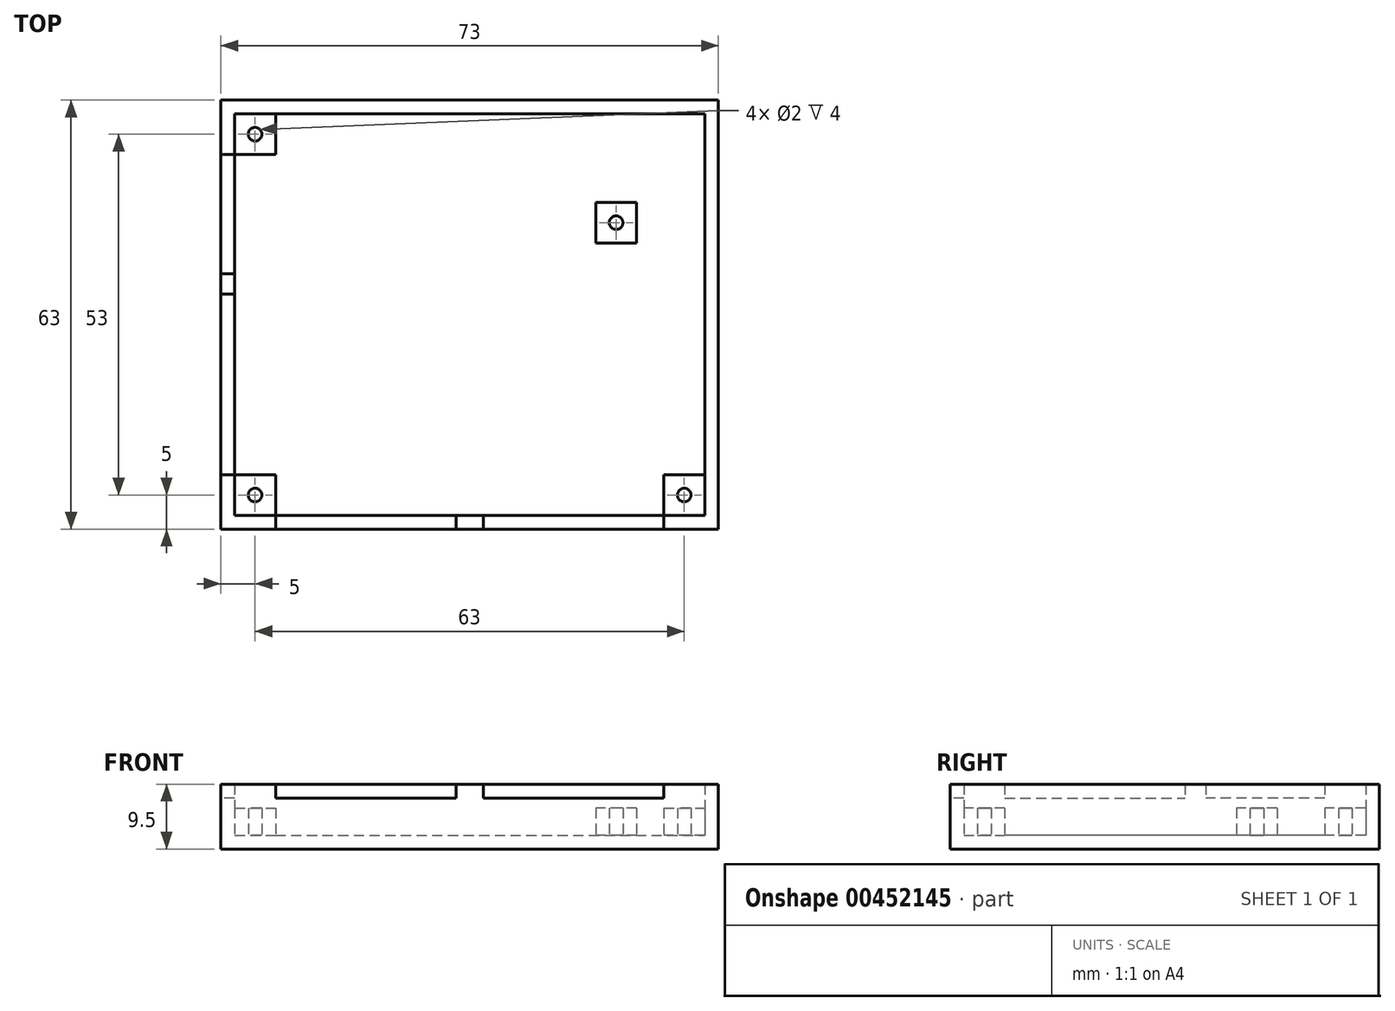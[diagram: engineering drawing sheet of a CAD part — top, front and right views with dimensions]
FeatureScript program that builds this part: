
annotation { "Feature Type Name" : "Feature", "Feature Type Description" : "" }
export const myFeature = defineFeature(function(context is Context, id is Id, definition is map)
    precondition{}
    {
        {
            assignVariable(context, id + "F0", {"name" : "SCREW_BOX_H", "anyValue" : 4});
        }
        {
            assignVariable(context, id + "F1", {"name" : "GPIO_H", "anyValue" : 2.5 * mm});
        }
        {
            assignVariable(context, id + "F2", {"name" : "PERIPHERALS_BOTTOM", "anyValue" : 7 * mm});
        }
        {
            var Q0;
            Q0=qCreatedBy(makeId("Top.planeOp"),FACE);
            var sketch = newSketch(context, id + "F3", { "sketchPlane" : qUnion([Q0])});
            skLineSegment(sketch, "E0.bottom", {"start": v(-34.5, 29.5) * mm, "end": v(34.5, 29.5) * mm});
            skLineSegment(sketch, "E0.top", {"start": v(-34.5, -29.5) * mm, "end": v(34.5, -29.5) * mm});
            skLineSegment(sketch, "E0.left", {"start": v(-34.5, 29.5) * mm, "end": v(-34.5, -29.5) * mm});
            skLineSegment(sketch, "E0.right", {"start": v(34.5, 29.5) * mm, "end": v(34.5, -29.5) * mm});
            skPoint(sketch, "E0.middle", {"position": v(0, 0) * mm});
            skLineSegment(sketch, "E1.0", {"start": v(-36.5, 31.5) * mm, "end": v(36.5, 31.5) * mm});
            skLineSegment(sketch, "E1.1", {"start": v(-36.5, 31.5) * mm, "end": v(-36.5, -31.5) * mm});
            skLineSegment(sketch, "E1.2", {"start": v(-36.5, -31.5) * mm, "end": v(36.5, -31.5) * mm});
            skLineSegment(sketch, "E1.3", {"start": v(36.5, 31.5) * mm, "end": v(36.5, -31.5) * mm});
            skSolve(sketch);
        }
        {
            var Q0;
            Q0=makeQuery(id+"F3.imprint","IMPRINT",FACE,{"disambiguationData":[TD([[makeQuery(id+"F3.imprint","IMPRINT",EDGE,{"derivedFrom":sQuery(id+"F3.wireOp",EDGE,"E0.bottom")}),1.0]])]});
            extrude(context, id + "F4", {"entities" : qUnion([Q0]), "depth" : getVariable(context, 'PERIPHERALS_BOTTOM') + getVariable(context, 'GPIO_H')});
        }
        {
            var Q0;
            Q0=makeQuery(id+"F3.imprint","IMPRINT",FACE,{"disambiguationData":[TD([[makeQuery(id+"F3.imprint","IMPRINT",EDGE,{"derivedFrom":sQuery(id+"F3.wireOp",EDGE,"E0.bottom")}),-1.0]])]});
            extrude(context, id + "F5", {"entities" : qUnion([Q0]), "operationType" : NewBodyOperationType.ADD, "depth" : 2 * mm});
        }
        {
            var Q0;
            Q0=makeQuery(id+"F5.opExtrude","CAP_FACE",FACE,{"disambiguationData":[OSD([sQuery(id+"F3.wireOp",EDGE,"E0.bottom"),sQuery(id+"F3.wireOp",EDGE,"E0.top"),sQuery(id+"F3.wireOp",EDGE,"E0.left"),sQuery(id+"F3.wireOp",EDGE,"E0.right")])],"isStart":false});
            var sketch = newSketch(context, id + "F6", { "sketchPlane" : qUnion([Q0])});
            skLineSegment(sketch, "E2.bottom", {"start": v(34.5, -29.5) * mm, "end": v(28.5, -29.5) * mm});
            skLineSegment(sketch, "E2.top", {"start": v(34.5, -23.5) * mm, "end": v(28.5, -23.5) * mm});
            skLineSegment(sketch, "E2.left", {"start": v(34.5, -29.5) * mm, "end": v(34.5, -23.5) * mm});
            skLineSegment(sketch, "E2.right", {"start": v(28.5, -29.5) * mm, "end": v(28.5, -23.5) * mm});
            skLineSegment(sketch, "E3.MirrorCS", {"start": v(-28.5, -29.5) * mm, "end": v(-28.5, -23.5) * mm});
            skLineSegment(sketch, "E4.MirrorCS", {"start": v(-34.5, -23.5) * mm, "end": v(-28.5, -23.5) * mm});
            skLineSegment(sketch, "E5.MirrorCS", {"start": v(-34.5, -29.5) * mm, "end": v(-34.5, -23.5) * mm});
            skLineSegment(sketch, "E6.MirrorCS", {"start": v(-34.5, -29.5) * mm, "end": v(-28.5, -29.5) * mm});
            skLineSegment(sketch, "E7.MirrorCS", {"start": v(-34.5, 23.5) * mm, "end": v(-28.5, 23.5) * mm});
            skLineSegment(sketch, "E8.MirrorCS", {"start": v(-28.5, 29.5) * mm, "end": v(-28.5, 23.5) * mm});
            skLineSegment(sketch, "E9.MirrorCS", {"start": v(-34.5, 29.5) * mm, "end": v(-28.5, 29.5) * mm});
            skLineSegment(sketch, "E10.MirrorCS", {"start": v(-34.5, 29.5) * mm, "end": v(-34.5, 23.5) * mm});
            skCircle(sketch, "E11", {"center": v(31.5, -26.5) * mm, "radius": 1 * mm});
            skPoint(sketch, "E11.centerSnap0", {"position": v(28.5, -26.5) * mm});
            skPoint(sketch, "E11.centerSnap1", {"position": v(31.5, -23.5) * mm});
            skCircle(sketch, "E12.MirrorC", {"center": v(-31.5, -26.5) * mm, "radius": 1 * mm});
            skCircle(sketch, "E13.MirrorC", {"center": v(-31.5, 26.5) * mm, "radius": 1 * mm});
            skLineSegment(sketch, "E14.top", {"start": v(34.5, 16.5) * mm, "end": v(24.5, 16.5) * mm, "construction": true});
            skLineSegment(sketch, "E14.right", {"start": v(24.5, 29.5) * mm, "end": v(24.5, 16.5) * mm, "construction": true});
            skLineSegment(sketch, "E15.bottom", {"start": v(24.5, 16.5) * mm, "end": v(18.5, 16.5) * mm});
            skLineSegment(sketch, "E15.top", {"start": v(24.5, 10.5) * mm, "end": v(18.5, 10.5) * mm});
            skLineSegment(sketch, "E15.left", {"start": v(24.5, 16.5) * mm, "end": v(24.5, 10.5) * mm});
            skLineSegment(sketch, "E15.right", {"start": v(18.5, 16.5) * mm, "end": v(18.5, 10.5) * mm});
            skCircle(sketch, "E16", {"center": v(21.5, 13.5) * mm, "radius": 1 * mm});
            skPoint(sketch, "E16.centerSnap0", {"position": v(21.5, 10.5) * mm});
            skPoint(sketch, "E16.centerSnap1", {"position": v(18.5, 13.5) * mm});
            skSolve(sketch);
        }
        {
            var Q0;
            Q0=makeQuery(id+"F6.imprint","IMPRINT",FACE,{"disambiguationData":[TD([[makeQuery(id+"F6.imprint","IMPRINT",EDGE,{"derivedFrom":sQuery(id+"F6.wireOp",EDGE,"E15.bottom")}),1.0]])]});
            var Q1;
            Q1=makeQuery(id+"F6.imprint","IMPRINT",FACE,{"disambiguationData":[TD([[makeQuery(id+"F6.imprint","IMPRINT",EDGE,{"derivedFrom":sQuery(id+"F6.wireOp",EDGE,"E2.bottom")}),1.0]])]});
            var Q2;
            Q2=makeQuery(id+"F6.imprint","IMPRINT",FACE,{"disambiguationData":[TD([[makeQuery(id+"F6.imprint","IMPRINT",EDGE,{"derivedFrom":sQuery(id+"F6.wireOp",EDGE,"E7.MirrorCS")}),1.0]])]});
            var Q3;
            Q3=makeQuery(id+"F6.imprint","IMPRINT",FACE,{"disambiguationData":[TD([[makeQuery(id+"F6.imprint","IMPRINT",EDGE,{"derivedFrom":sQuery(id+"F6.wireOp",EDGE,"E3.MirrorCS")}),1.0]])]});
            extrude(context, id + "F7", {"entities" : qUnion([Q0, Q1, Q2, Q3]), "operationType" : NewBodyOperationType.ADD, "depth" : (getVariable(context, 'SCREW_BOX_H')) * mm});
        }
        {
            var Q0;
            Q0=makeQuery(id+"F4.opExtrude","SWEPT_FACE",FACE,{"disambiguationData":[OSD([sQuery(id+"F3.wireOp",EDGE,"E1.2")])]});
            var sketch = newSketch(context, id + "F8", { "sketchPlane" : qUnion([Q0])});
            skLineSegment(sketch, "E17.bottom", {"start": v(28.5, 9.5) * mm, "end": v(2, 9.5) * mm});
            skLineSegment(sketch, "E17.top", {"start": v(28.5, 7.5) * mm, "end": v(2, 7.5) * mm});
            skLineSegment(sketch, "E17.left", {"start": v(28.5, 9.5) * mm, "end": v(28.5, 7.5) * mm});
            skLineSegment(sketch, "E17.right", {"start": v(2, 9.5) * mm, "end": v(2, 7.5) * mm});
            skLineSegment(sketch, "E18.0.0", {"start": v(-28.5, 2) * mm, "end": v(-28.5, 6) * mm, "construction": true});
            skLineSegment(sketch, "E18.0.1", {"start": v(-28.5, 6) * mm, "end": v(-34.5, 6) * mm, "construction": true});
            skLineSegment(sketch, "E18.0.2", {"start": v(-34.5, 6) * mm, "end": v(-34.5, 9.5) * mm, "construction": true});
            skLineSegment(sketch, "E18.0.3", {"start": v(-34.5, 9.5) * mm, "end": v(34.5, 9.5) * mm, "construction": true});
            skLineSegment(sketch, "E18.0.4", {"start": v(34.5, 9.5) * mm, "end": v(34.5, 6) * mm, "construction": true});
            skLineSegment(sketch, "E18.0.5", {"start": v(34.5, 6) * mm, "end": v(28.5, 6) * mm, "construction": true});
            skLineSegment(sketch, "E18.0.6", {"start": v(28.5, 6) * mm, "end": v(28.5, 2) * mm, "construction": true});
            skLineSegment(sketch, "E18.0.7", {"start": v(28.5, 2) * mm, "end": v(-28.5, 2) * mm, "construction": true});
            skLineSegment(sketch, "E19", {"start": v(0, 9.5) * mm, "end": v(0, 0) * mm, "construction": true});
            skLineSegment(sketch, "E20.MirrorCS", {"start": v(-2, 9.5) * mm, "end": v(-2, 7.5) * mm});
            skLineSegment(sketch, "E21.MirrorCS", {"start": v(-28.5, 7.5) * mm, "end": v(-2, 7.5) * mm});
            skLineSegment(sketch, "E22.MirrorCS", {"start": v(-28.5, 9.5) * mm, "end": v(-28.5, 7.5) * mm});
            skSolve(sketch);
        }
        {
            var Q0;
            Q0=makeQuery(id+"F8.imprint","IMPRINT",FACE,{"disambiguationData":[TD([[makeQuery(id+"F8.imprint","IMPRINT",EDGE,{"derivedFrom":sQuery(id+"F8.wireOp",EDGE,"E17.bottom")}),-1.0]])]});
            var Q1;
            {var subQ0=sQuery(id+"F8.wireOp",EDGE,"E20.MirrorCS");Q1=makeQuery(id+"F8.imprint","IMPRINT",FACE,{"disambiguationData":[TD([[makeQuery(id+"F8.imprint","IMPRINT",EDGE,{"derivedFrom":subQ0}),-1.0]])]});}
            extrude(context, id + "F9", {"entities" : qUnion([Q0, Q1]), "operationType" : NewBodyOperationType.REMOVE, "endBound" : BoundingType.UP_TO_NEXT, "oppositeDirection" : true, "depth" : 25 * mm});
        }
        {
            var Q0;
            Q0=makeQuery(id+"F4.opExtrude","SWEPT_FACE",FACE,{"disambiguationData":[OSD([sQuery(id+"F3.wireOp",EDGE,"E1.1")])]});
            var sketch = newSketch(context, id + "F10", { "sketchPlane" : qUnion([Q0])});
            skLineSegment(sketch, "E23.bottom", {"start": v(23.5, 9.5) * mm, "end": v(-3, 9.5) * mm});
            skLineSegment(sketch, "E23.top", {"start": v(23.5, 7.5) * mm, "end": v(-3, 7.5) * mm});
            skLineSegment(sketch, "E23.left", {"start": v(23.5, 9.5) * mm, "end": v(23.5, 7.5) * mm});
            skLineSegment(sketch, "E23.right", {"start": v(-3, 9.5) * mm, "end": v(-3, 7.5) * mm});
            skLineSegment(sketch, "E24.bottom", {"start": v(-23.5, 9.5) * mm, "end": v(-6, 9.5) * mm});
            skLineSegment(sketch, "E24.top", {"start": v(-23.5, 7.5) * mm, "end": v(-6, 7.5) * mm});
            skLineSegment(sketch, "E24.left", {"start": v(-23.5, 9.5) * mm, "end": v(-23.5, 7.5) * mm});
            skLineSegment(sketch, "E24.right", {"start": v(-6, 9.5) * mm, "end": v(-6, 7.5) * mm});
            skLineSegment(sketch, "E25.0.0", {"start": v(-23.5, 2) * mm, "end": v(-23.5, 6) * mm, "construction": true});
            skLineSegment(sketch, "E25.0.1", {"start": v(-23.5, 6) * mm, "end": v(-29.5, 6) * mm, "construction": true});
            skLineSegment(sketch, "E25.0.2", {"start": v(-29.5, 6) * mm, "end": v(-29.5, 9.5) * mm, "construction": true});
            skLineSegment(sketch, "E25.0.3", {"start": v(-29.5, 9.5) * mm, "end": v(29.5, 9.5) * mm, "construction": true});
            skLineSegment(sketch, "E25.0.4", {"start": v(29.5, 9.5) * mm, "end": v(29.5, 6) * mm});
            skLineSegment(sketch, "E25.0.5", {"start": v(29.5, 6) * mm, "end": v(23.5, 6) * mm, "construction": true});
            skLineSegment(sketch, "E25.0.6", {"start": v(23.5, 6) * mm, "end": v(23.5, 2) * mm, "construction": true});
            skLineSegment(sketch, "E25.0.7", {"start": v(23.5, 2) * mm, "end": v(-23.5, 2) * mm, "construction": true});
            skSolve(sketch);
        }
        {
            var Q0;
            Q0=makeQuery(id+"F10.imprint","IMPRINT",FACE,{"disambiguationData":[TD([[makeQuery(id+"F10.imprint","IMPRINT",EDGE,{"derivedFrom":sQuery(id+"F10.wireOp",EDGE,"E23.bottom")}),-1.0]])]});
            var Q1;
            Q1=makeQuery(id+"F10.imprint","IMPRINT",FACE,{"disambiguationData":[TD([[makeQuery(id+"F10.imprint","IMPRINT",EDGE,{"derivedFrom":sQuery(id+"F10.wireOp",EDGE,"E24.bottom")}),-1.0]])]});
            extrude(context, id + "F11", {"entities" : qUnion([Q0, Q1]), "operationType" : NewBodyOperationType.REMOVE, "endBound" : BoundingType.UP_TO_NEXT, "oppositeDirection" : true, "depth" : 25 * mm});
        }
    });
